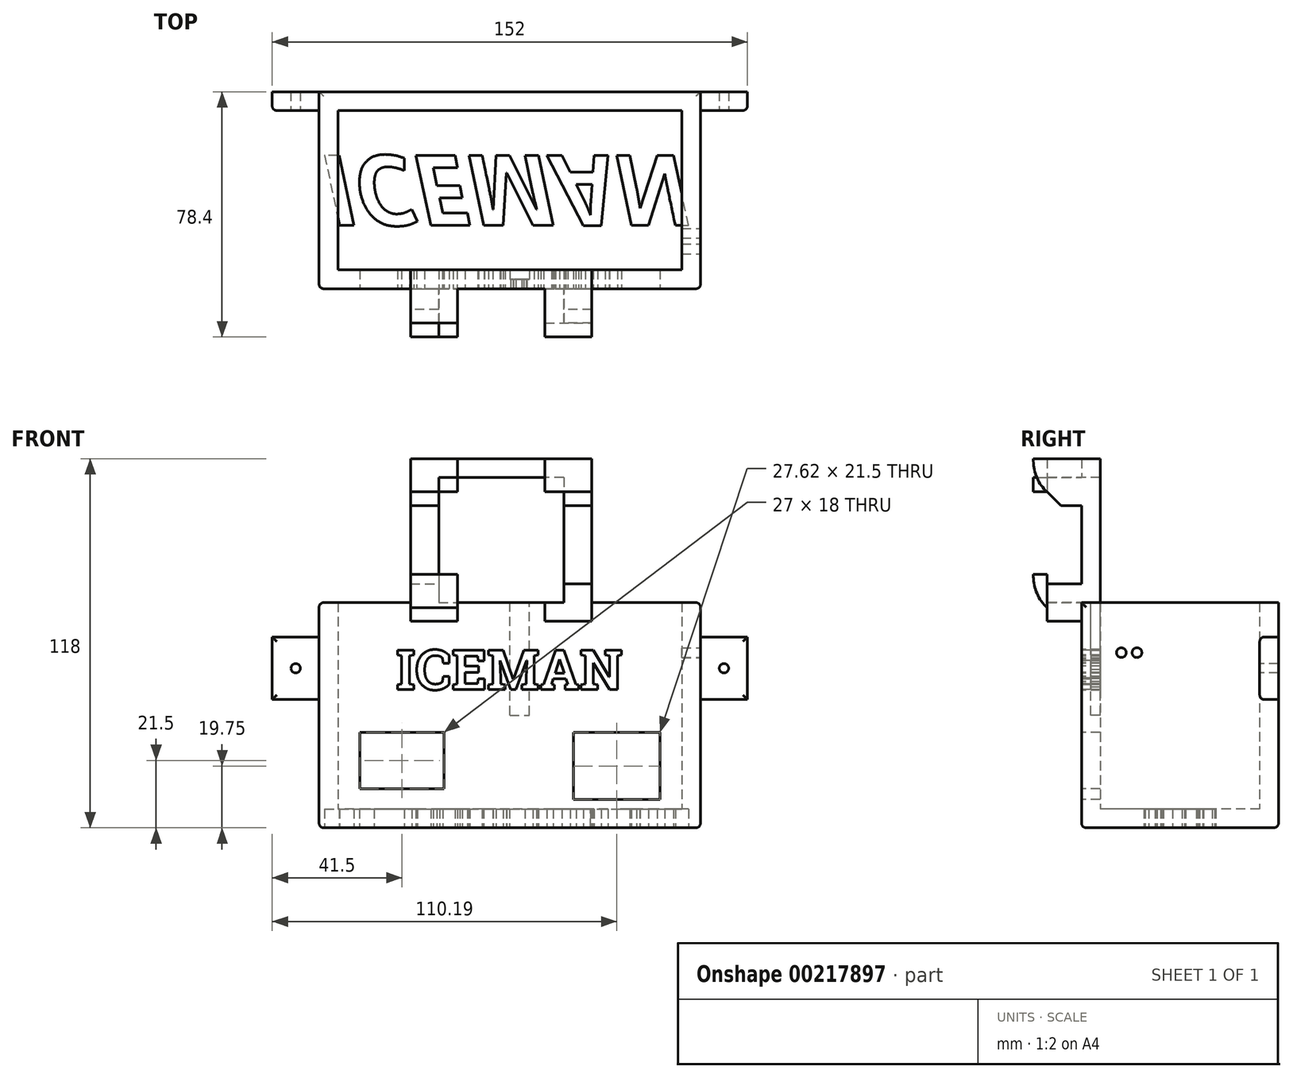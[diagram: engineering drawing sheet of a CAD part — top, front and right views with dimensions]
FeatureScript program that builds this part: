
annotation { "Feature Type Name" : "Feature", "Feature Type Description" : "" }
export const myFeature = defineFeature(function(context is Context, id is Id, definition is map)
    precondition{}
    {
        {
            var Q0;
            Q0=qCreatedBy(makeId("Top.planeOp"),FACE);
            var sketch = newSketch(context, id + "F0", { "sketchPlane" : qUnion([Q0])});
            skLineSegment(sketch, "E0.bottom", {"start": v(-61, 31.5) * mm, "end": v(61, 31.5) * mm});
            skLineSegment(sketch, "E0.top", {"start": v(-61, -31.5) * mm, "end": v(61, -31.5) * mm});
            skLineSegment(sketch, "E0.left", {"start": v(-61, 31.5) * mm, "end": v(-61, -31.5) * mm});
            skLineSegment(sketch, "E0.right", {"start": v(61, 31.5) * mm, "end": v(61, -31.5) * mm});
            skPoint(sketch, "E0.middle", {"position": v(0, 0) * mm});
            skSolve(sketch);
        }
        {
            var Q0;
            Q0 = qSketchRegion(id + "F0", true);
            extrude(context, id + "F1", {"entities" : qUnion([Q0]), "depth" : 6 * mm});
        }
        {
            var Q0;
            Q0=makeQuery(id+"F1.opExtrude","CAP_FACE",FACE,{"disambiguationData":[OSD([sQuery(id+"F0.wireOp",EDGE,"E0.bottom"),sQuery(id+"F0.wireOp",EDGE,"E0.top"),sQuery(id+"F0.wireOp",EDGE,"E0.left"),sQuery(id+"F0.wireOp",EDGE,"E0.right")])],"isStart":false});
            var sketch = newSketch(context, id + "F2", { "sketchPlane" : qUnion([Q0])});
            skLineSegment(sketch, "E1", {"start": v(-55, 25.5) * mm, "end": v(-55, -25.5) * mm});
            skLineSegment(sketch, "E2", {"start": v(-55, -25.5) * mm, "end": v(55, -25.5) * mm});
            skLineSegment(sketch, "E3", {"start": v(55, 25.5) * mm, "end": v(-55, 25.5) * mm});
            skLineSegment(sketch, "E4", {"start": v(55, 25.5) * mm, "end": v(55, -25.5) * mm});
            skPoint(sketch, "E5.orphan", {"position": v(55, -31.5) * mm});
            skLineSegment(sketch, "E6.bottom", {"start": v(-61, 31.5) * mm, "end": v(61, 31.5) * mm});
            skLineSegment(sketch, "E6.top", {"start": v(-61, -31.5) * mm, "end": v(61, -31.5) * mm});
            skLineSegment(sketch, "E6.left", {"start": v(-61, 31.5) * mm, "end": v(-61, -31.5) * mm});
            skLineSegment(sketch, "E6.right", {"start": v(61, 31.5) * mm, "end": v(61, -31.5) * mm});
            skSolve(sketch);
        }
        {
            var Q0;
            Q0 = qSketchRegion(id + "F2", true);
            extrude(context, id + "F3", {"entities" : qUnion([Q0]), "operationType" : NewBodyOperationType.ADD, "depth" : 66 * mm});
        }
        {
            var Q0;
            Q0=makeQuery(id+"F3.boolean.opBoolean","MERGE",FACE,{"derivedFrom":[makeQuery(id+"F1.opExtrude","SWEPT_FACE",FACE,{"disambiguationData":[OSD([sQuery(id+"F0.wireOp",EDGE,"E0.top")])]}),makeQuery(id+"F3.opExtrude","SWEPT_FACE",FACE,{"disambiguationData":[OSD([sQuery(id+"F2.wireOp",EDGE,"E6.top")])]})]});
            var sketch = newSketch(context, id + "F4", { "sketchPlane" : qUnion([Q0])});
            skLineSegment(sketch, "E7.bottom", {"start": v(48, 30.5) * mm, "end": v(20.38, 30.5) * mm});
            skLineSegment(sketch, "E7.top", {"start": v(48, 9) * mm, "end": v(20.38, 9) * mm});
            skLineSegment(sketch, "E7.left", {"start": v(48, 30.5) * mm, "end": v(48, 9) * mm});
            skLineSegment(sketch, "E7.right", {"start": v(20.38, 30.5) * mm, "end": v(20.38, 9) * mm});
            skLineSegment(sketch, "E8.bottom", {"start": v(-48, 30.5) * mm, "end": v(-21, 30.5) * mm});
            skLineSegment(sketch, "E8.top", {"start": v(-48, 12.5) * mm, "end": v(-21, 12.5) * mm});
            skLineSegment(sketch, "E8.left", {"start": v(-48, 30.5) * mm, "end": v(-48, 12.5) * mm});
            skLineSegment(sketch, "E8.right", {"start": v(-21, 30.5) * mm, "end": v(-21, 12.5) * mm});
            skText(sketch, "E9", { "text": "ICEMAN", "fontName": "RobotoSlab-Bold.ttf"});
            const initialGuessF4  = {"E9": [-0.03643, 0.04416, 1, 0, 0.01284]};
            skSetInitialGuess(sketch, initialGuessF4);
            skSolve(sketch);
        }
        {
            var Q0;
            Q0 = qSketchRegion(id + "F4", true);
            extrude(context, id + "F5", {"entities" : qUnion([Q0]), "operationType" : NewBodyOperationType.REMOVE, "oppositeDirection" : true, "depth" : 6 * mm});
        }
        {
            var Q0;
            Q0=makeQuery(id+"F1.opExtrude","CAP_FACE",FACE,{"disambiguationData":[OSD([sQuery(id+"F0.wireOp",EDGE,"E0.bottom"),sQuery(id+"F0.wireOp",EDGE,"E0.top"),sQuery(id+"F0.wireOp",EDGE,"E0.left"),sQuery(id+"F0.wireOp",EDGE,"E0.right")])],"isStart":true});
            var sketch = newSketch(context, id + "F6", { "sketchPlane" : qUnion([Q0])});
            skPoint(sketch, "E10.bottom.start.orphan", {"position": v(42.45, 0) * mm});
            skText(sketch, "E11", { "text": "ICEMAN", "fontName": "OpenSans-BoldItalic.ttf"});
            const initialGuessF6  = {"E11": [-0.06005, -0.01114, 1, 0, 0.02254]};
            skSetInitialGuess(sketch, initialGuessF6);
            skSolve(sketch);
        }
        {
            var Q0;
            Q0 = qSketchRegion(id + "F6", true);
            extrude(context, id + "F7", {"entities" : qUnion([Q0]), "operationType" : NewBodyOperationType.REMOVE, "oppositeDirection" : true, "depth" : 6 * mm});
        }
        {
            var Q0;
            Q0=makeQuery(id+"F3.boolean.opBoolean","MERGE",FACE,{"derivedFrom":[makeQuery(id+"F1.opExtrude","SWEPT_FACE",FACE,{"disambiguationData":[OSD([sQuery(id+"F0.wireOp",EDGE,"E0.right")])]}),makeQuery(id+"F3.opExtrude","SWEPT_FACE",FACE,{"disambiguationData":[OSD([sQuery(id+"F2.wireOp",EDGE,"E6.right")])]})]});
            var sketch = newSketch(context, id + "F8", { "sketchPlane" : qUnion([Q0])});
            skCircle(sketch, "E12", {"center": v(-18.77, 56) * mm, "radius": 1.55 * mm});
            skLineSegment(sketch, "E13", {"start": v(-18.77, 56) * mm, "end": v(33.66, 56) * mm, "construction": true});
            skCircle(sketch, "E14", {"center": v(-13.77, 56) * mm, "radius": 1.55 * mm, "construction": true});
            skCircle(sketch, "E15", {"center": v(-13.77, 56) * mm, "radius": 1.56 * mm});
            skSolve(sketch);
        }
        {
            var Q0;
            Q0 = qSketchRegion(id + "F8", true);
            extrude(context, id + "F9", {"entities" : qUnion([Q0]), "operationType" : NewBodyOperationType.REMOVE, "oppositeDirection" : true, "depth" : 6 * mm});
        }
        {
            var Q0;
            Q0=makeQuery(id+"F3.boolean.opBoolean","MERGE",FACE,{"derivedFrom":[makeQuery(id+"F1.opExtrude","SWEPT_FACE",FACE,{"disambiguationData":[OSD([sQuery(id+"F0.wireOp",EDGE,"E0.right")])]}),makeQuery(id+"F3.opExtrude","SWEPT_FACE",FACE,{"disambiguationData":[OSD([sQuery(id+"F2.wireOp",EDGE,"E6.right")])]})]});
            var sketch = newSketch(context, id + "F10", { "sketchPlane" : qUnion([Q0])});
            skLineSegment(sketch, "E16.bottom", {"start": v(31.5, 61) * mm, "end": v(25.5, 61) * mm});
            skLineSegment(sketch, "E16.top", {"start": v(31.5, 41) * mm, "end": v(25.5, 41) * mm});
            skLineSegment(sketch, "E16.left", {"start": v(31.5, 61) * mm, "end": v(31.5, 41) * mm});
            skLineSegment(sketch, "E16.right", {"start": v(25.5, 61) * mm, "end": v(25.5, 41) * mm});
            skLineSegment(sketch, "E17", {"start": v(31.5, 61) * mm, "end": v(-91.25, 61) * mm, "construction": true});
            skLineSegment(sketch, "E18", {"start": v(-91.25, 61) * mm, "end": v(31.5, 41) * mm, "construction": true});
            skLineSegment(sketch, "E19", {"start": v(31.5, 41) * mm, "end": v(-54.22, 41) * mm, "construction": true});
            skLineSegment(sketch, "E20", {"start": v(-54.22, 41) * mm, "end": v(-136.07, 61) * mm, "construction": true});
            skSolve(sketch);
        }
        {
            var Q0;
            Q0 = qSketchRegion(id + "F10", true);
            extrude(context, id + "F11", {"entities" : qUnion([Q0]), "operationType" : NewBodyOperationType.ADD, "depth" : 15 * mm});
        }
        {
            var Q0;
            Q0=makeQuery(id+"F3.boolean.opBoolean","MERGE",FACE,{"derivedFrom":[makeQuery(id+"F1.opExtrude","SWEPT_FACE",FACE,{"disambiguationData":[OSD([sQuery(id+"F0.wireOp",EDGE,"E0.left")])]}),makeQuery(id+"F3.opExtrude","SWEPT_FACE",FACE,{"disambiguationData":[OSD([sQuery(id+"F2.wireOp",EDGE,"E6.left")])]})]});
            var sketch = newSketch(context, id + "F12", { "sketchPlane" : qUnion([Q0])});
            skLineSegment(sketch, "E21.bottom", {"start": v(-31.5, 61) * mm, "end": v(-25.5, 61) * mm});
            skLineSegment(sketch, "E21.top", {"start": v(-31.5, 41) * mm, "end": v(-25.5, 41) * mm});
            skLineSegment(sketch, "E21.left", {"start": v(-31.5, 61) * mm, "end": v(-31.5, 41) * mm});
            skLineSegment(sketch, "E21.right", {"start": v(-25.5, 61) * mm, "end": v(-25.5, 41) * mm});
            skSolve(sketch);
        }
        {
            var Q0;
            Q0 = qSketchRegion(id + "F12", true);
            extrude(context, id + "F13", {"entities" : qUnion([Q0]), "operationType" : NewBodyOperationType.ADD, "depth" : 15 * mm});
        }
        {
            var Q0;
            Q0=makeQuery(id+"F13.opExtrude","SWEPT_FACE",FACE,{"disambiguationData":[OSD([sQuery(id+"F12.wireOp",EDGE,"E21.right")])]});
            var sketch = newSketch(context, id + "F14", { "sketchPlane" : qUnion([Q0])});
            skCircle(sketch, "E22", {"center": v(-68.5, 51) * mm, "radius": 1.5 * mm});
            skPoint(sketch, "E22.centerSnap0", {"position": v(-68.5, 61) * mm});
            skPoint(sketch, "E22.centerSnap1", {"position": v(-76, 51) * mm});
            skSolve(sketch);
        }
        {
            var Q0;
            Q0 = qSketchRegion(id + "F14", true);
            extrude(context, id + "F15", {"entities" : qUnion([Q0]), "operationType" : NewBodyOperationType.REMOVE, "endBound" : BoundingType.THROUGH_ALL, "oppositeDirection" : true, "depth" : 25 * mm});
        }
        {
            var Q0;
            Q0=makeQuery(id+"F11.opExtrude","SWEPT_FACE",FACE,{"disambiguationData":[OSD([sQuery(id+"F10.wireOp",EDGE,"E16.right")])]});
            var sketch = newSketch(context, id + "F16", { "sketchPlane" : qUnion([Q0])});
            skCircle(sketch, "E23", {"center": v(68.5, 51) * mm, "radius": 1.5 * mm});
            skPoint(sketch, "E23.centerSnap0", {"position": v(68.5, 61) * mm});
            skPoint(sketch, "E23.centerSnap1", {"position": v(76, 51) * mm});
            skSolve(sketch);
        }
        {
            var Q0;
            Q0 = qSketchRegion(id + "F16", true);
            extrude(context, id + "F17", {"entities" : qUnion([Q0]), "operationType" : NewBodyOperationType.ADD, "endBound" : BoundingType.THROUGH_ALL, "depth" : 25 * mm});
        }
        {
            var Q0;
            Q0=makeQuery(id+"F17.opExtrude","CAP_FACE",FACE,{"disambiguationData":[OSD([sQuery(id+"F16.wireOp",EDGE,"E23")])],"isStart":false});
            extrude(context, id + "F18", {"entities" : qUnion([Q0]), "operationType" : NewBodyOperationType.REMOVE, "endBound" : BoundingType.THROUGH_ALL, "oppositeDirection" : true, "depth" : 25 * mm});
        }
        {
            var Q0;
            Q0=makeQuery(id+"F3.opExtrude","CAP_FACE",FACE,{"disambiguationData":[OSD([sQuery(id+"F2.wireOp",EDGE,"E1"),sQuery(id+"F2.wireOp",EDGE,"E2"),sQuery(id+"F2.wireOp",EDGE,"E3"),sQuery(id+"F2.wireOp",EDGE,"E4"),sQuery(id+"F2.wireOp",EDGE,"E6.bottom"),sQuery(id+"F2.wireOp",EDGE,"E6.top"),sQuery(id+"F2.wireOp",EDGE,"E6.left"),sQuery(id+"F2.wireOp",EDGE,"E6.right")])],"isStart":false});
            var sketch = newSketch(context, id + "F19", { "sketchPlane" : qUnion([Q0])});
            skLineSegment(sketch, "E24.bottom", {"start": v(0, -25.5) * mm, "end": v(6.26, -25.5) * mm});
            skLineSegment(sketch, "E24.top", {"start": v(0, -28.5) * mm, "end": v(6.26, -28.5) * mm});
            skLineSegment(sketch, "E24.left", {"start": v(0, -25.5) * mm, "end": v(0, -28.5) * mm});
            skLineSegment(sketch, "E24.right", {"start": v(6.26, -25.5) * mm, "end": v(6.26, -28.5) * mm});
            skSolve(sketch);
        }
        {
            var Q0;
            Q0=makeQuery(id+"F19.imprint","IMPRINT",FACE,{"disambiguationData":[TD([[makeQuery(id+"F19.imprint","IMPRINT",EDGE,{"derivedFrom":sQuery(id+"F19.wireOp",EDGE,"E24.bottom")}),-1.0]])]});
            extrude(context, id + "F20", {"entities" : qUnion([Q0]), "operationType" : NewBodyOperationType.REMOVE, "oppositeDirection" : true, "depth" : 36 * mm});
        }
        {
            var Q0;
            Q0=makeQuery(id+"F3.opExtrude","CAP_FACE",FACE,{"disambiguationData":[OSD([sQuery(id+"F2.wireOp",EDGE,"E1"),sQuery(id+"F2.wireOp",EDGE,"E2"),sQuery(id+"F2.wireOp",EDGE,"E3"),sQuery(id+"F2.wireOp",EDGE,"E4"),sQuery(id+"F2.wireOp",EDGE,"E6.bottom"),sQuery(id+"F2.wireOp",EDGE,"E6.top"),sQuery(id+"F2.wireOp",EDGE,"E6.left"),sQuery(id+"F2.wireOp",EDGE,"E6.right")])],"isStart":false});
            var sketch = newSketch(context, id + "F21", { "sketchPlane" : qUnion([Q0])});
            skLineSegment(sketch, "E25.bottom", {"start": v(17.26, -25.5) * mm, "end": v(26.26, -25.5) * mm});
            skLineSegment(sketch, "E25.top", {"start": v(17.26, -31.5) * mm, "end": v(26.26, -31.5) * mm});
            skLineSegment(sketch, "E25.left", {"start": v(17.26, -25.5) * mm, "end": v(17.26, -31.5) * mm});
            skLineSegment(sketch, "E25.right", {"start": v(26.26, -25.5) * mm, "end": v(26.26, -31.5) * mm});
            skLineSegment(sketch, "E26.bottom", {"start": v(-31.74, -25.5) * mm, "end": v(-22.74, -25.5) * mm});
            skLineSegment(sketch, "E26.top", {"start": v(-31.74, -31.5) * mm, "end": v(-22.74, -31.5) * mm});
            skLineSegment(sketch, "E26.left", {"start": v(-31.74, -25.5) * mm, "end": v(-31.74, -31.5) * mm});
            skLineSegment(sketch, "E26.right", {"start": v(-22.74, -25.5) * mm, "end": v(-22.74, -31.5) * mm});
            skSolve(sketch);
        }
        {
            var Q0;
            Q0 = qSketchRegion(id + "F21", true);
            extrude(context, id + "F22", {"entities" : qUnion([Q0]), "operationType" : NewBodyOperationType.ADD, "depth" : 46 * mm});
        }
        {
            var Q0;
            Q0=makeQuery(id+"F22.opExtrude","SWEPT_FACE",FACE,{"disambiguationData":[OSD([sQuery(id+"F21.wireOp",EDGE,"E26.right")])]});
            var sketch = newSketch(context, id + "F23", { "sketchPlane" : qUnion([Q0])});
            skLineSegment(sketch, "E27.bottom", {"start": v(-25.5, 118) * mm, "end": v(-31.5, 118) * mm});
            skLineSegment(sketch, "E27.top", {"start": v(-25.5, 112) * mm, "end": v(-31.5, 112) * mm});
            skLineSegment(sketch, "E27.left", {"start": v(-25.5, 118) * mm, "end": v(-25.5, 112) * mm});
            skLineSegment(sketch, "E27.right", {"start": v(-31.5, 118) * mm, "end": v(-31.5, 112) * mm});
            skSolve(sketch);
        }
        {
            var Q0;
            Q0 = qSketchRegion(id + "F23", true);
            extrude(context, id + "F24", {"entities" : qUnion([Q0]), "operationType" : NewBodyOperationType.ADD, "depth" : 44 * mm});
        }
        {
            var Q0;
            {var subQ2=sQuery(id+"F0.wireOp",EDGE,"E0.left");var subQ3=sQuery(id+"F0.wireOp",EDGE,"E0.top");var subQ5=sQuery(id+"F2.wireOp",EDGE,"E6.top");Q0=makeQuery(id+"F24.boolean.opBoolean","MERGE",FACE,{"derivedFrom":[makeQuery(id+"F22.boolean.opBoolean","MERGE",FACE,{"derivedFrom":[makeQuery(id+"F5.boolean.opBoolean","SPLIT",FACE,{"disambiguationData":[TD([makeQuery(id+"F1.opExtrude","SWEPT_FACE",FACE,{"disambiguationData":[OSD([subQ2])]})])],"derivedFrom":makeQuery(id+"F3.boolean.opBoolean","MERGE",FACE,{"derivedFrom":[makeQuery(id+"F1.opExtrude","SWEPT_FACE",FACE,{"disambiguationData":[OSD([subQ3])]}),makeQuery(id+"F3.opExtrude","SWEPT_FACE",FACE,{"disambiguationData":[OSD([subQ5])]})]})}),makeQuery(id+"F22.opExtrude","SWEPT_FACE",FACE,{"disambiguationData":[OSD([sQuery(id+"F21.wireOp",EDGE,"E25.top")])]}),makeQuery(id+"F22.opExtrude","SWEPT_FACE",FACE,{"disambiguationData":[OSD([sQuery(id+"F21.wireOp",EDGE,"E26.top")])]})]}),makeQuery(id+"F24.opExtrude","SWEPT_FACE",FACE,{"disambiguationData":[OSD([sQuery(id+"F23.wireOp",EDGE,"E27.right")])]})]});}
            var sketch = newSketch(context, id + "F25", { "sketchPlane" : qUnion([Q0])});
            skLineSegment(sketch, "E28.bottom", {"start": v(-31.74, 118) * mm, "end": v(-22.74, 118) * mm});
            skLineSegment(sketch, "E28.top", {"start": v(-31.74, 103) * mm, "end": v(-22.74, 103) * mm});
            skLineSegment(sketch, "E28.left", {"start": v(-31.74, 118) * mm, "end": v(-31.74, 103) * mm});
            skLineSegment(sketch, "E28.right", {"start": v(-22.74, 118) * mm, "end": v(-22.74, 103) * mm});
            skLineSegment(sketch, "E29", {"start": v(-2.74, 118) * mm, "end": v(-2.74, 63.41) * mm, "construction": true});
            skPoint(sketch, "E29.endSnap0", {"position": v(-2.74, 72) * mm});
            skLineSegment(sketch, "E30.MirrorCS", {"start": v(26.26, 103) * mm, "end": v(17.26, 103) * mm});
            skLineSegment(sketch, "E31.top", {"start": v(-31.74, 78) * mm, "end": v(-22.74, 78) * mm});
            skLineSegment(sketch, "E31.left", {"start": v(-31.74, 72) * mm, "end": v(-31.74, 78) * mm});
            skLineSegment(sketch, "E31.right", {"start": v(-22.74, 72) * mm, "end": v(-22.74, 78) * mm});
            skLineSegment(sketch, "E32.bottom", {"start": v(-22.74, 72) * mm, "end": v(17.26, 72) * mm});
            skLineSegment(sketch, "E32.top", {"start": v(-31.74, 66) * mm, "end": v(26.26, 66) * mm});
            skLineSegment(sketch, "E32.left", {"start": v(-31.74, 72) * mm, "end": v(-31.74, 66) * mm});
            skLineSegment(sketch, "E32.right", {"start": v(26.26, 72) * mm, "end": v(26.26, 66) * mm});
            skLineSegment(sketch, "E33.MirrorCS", {"start": v(26.26, 78) * mm, "end": v(17.26, 78) * mm});
            skLineSegment(sketch, "E34.bottom", {"start": v(-22.74, 72) * mm, "end": v(-16.74, 72) * mm});
            skLineSegment(sketch, "E34.top", {"start": v(-22.74, 66) * mm, "end": v(-16.74, 66) * mm});
            skLineSegment(sketch, "E34.right", {"start": v(-16.74, 72) * mm, "end": v(-16.74, 66) * mm});
            skLineSegment(sketch, "E35.MirrorCS", {"start": v(17.26, 112) * mm, "end": v(17.26, 103) * mm});
            skLineSegment(sketch, "E36.MirrorCS", {"start": v(17.26, 72) * mm, "end": v(17.26, 78) * mm});
            skLineSegment(sketch, "E37.MirrorCS", {"start": v(26.26, 72) * mm, "end": v(26.26, 78) * mm});
            skLineSegment(sketch, "E38.MirrorCS", {"start": v(26.26, 66) * mm, "end": v(11.26, 66) * mm});
            skLineSegment(sketch, "E39.MirrorCS", {"start": v(11.26, 72) * mm, "end": v(11.26, 66) * mm});
            skLineSegment(sketch, "E40.MirrorCS", {"start": v(-16.74, 72) * mm, "end": v(-22.74, 72) * mm});
            skPoint(sketch, "E41.orphan", {"position": v(-31.74, 72) * mm});
            skPoint(sketch, "E42.orphan", {"position": v(26.26, 72) * mm});
            skLineSegment(sketch, "E43.bottom", {"start": v(-22.74, 118) * mm, "end": v(-16.74, 118) * mm});
            skLineSegment(sketch, "E43.top", {"start": v(-22.74, 112) * mm, "end": v(-16.74, 112) * mm});
            skLineSegment(sketch, "E43.right", {"start": v(-16.74, 118) * mm, "end": v(-16.74, 112) * mm});
            skLineSegment(sketch, "E44.bottom", {"start": v(17.26, 118) * mm, "end": v(11.26, 118) * mm});
            skLineSegment(sketch, "E44.top", {"start": v(17.26, 112) * mm, "end": v(11.26, 112) * mm});
            skLineSegment(sketch, "E44.left", {"start": v(17.26, 118) * mm, "end": v(17.26, 112) * mm});
            skLineSegment(sketch, "E44.right", {"start": v(11.26, 118) * mm, "end": v(11.26, 112) * mm});
            skPoint(sketch, "E45.MirrorCS.end.orphan", {"position": v(17.26, 66) * mm});
            skPoint(sketch, "E45.MirrorCS.start.orphan", {"position": v(17.26, 72) * mm});
            skLineSegment(sketch, "E46.trimOffspring", {"start": v(-16.74, 66) * mm, "end": v(-31.74, 66) * mm});
            skSolve(sketch);
        }
        {
            var Q0;
            {var subQ2=sQuery(id+"F25.wireOp",EDGE,"E28.bottom");Q0=makeQuery(id+"F25.imprint","IMPRINT",FACE,{"disambiguationData":[TD([[makeQuery(id+"F25.imprint","IMPRINT",EDGE,{"derivedFrom":subQ2}),-1.0]])]});}
            var Q1;
            {var subQ2=sQuery(id+"F25.wireOp",EDGE,"E43.bottom");Q1=makeQuery(id+"F25.imprint","IMPRINT",FACE,{"disambiguationData":[TD([[makeQuery(id+"F25.imprint","IMPRINT",EDGE,{"derivedFrom":subQ2}),-1.0]])]});}
            var Q2;
            Q2=makeQuery(id+"F25.imprint","IMPRINT",FACE,{"disambiguationData":[TD([[makeQuery(id+"F25.imprint","IMPRINT",EDGE,{"derivedFrom":sQuery(id+"F25.wireOp",EDGE,"E44.bottom")}),-1.0]])]});
            var Q3;
            Q3=makeQuery(id+"F25.imprint","IMPRINT",FACE,{"disambiguationData":[TD([[makeQuery(id+"F25.imprint","IMPRINT",EDGE,{"derivedFrom":sQuery(id+"F25.wireOp",EDGE,"E31.top")}),-1.0]])]});
            var Q4;
            Q4=makeQuery(id+"F25.imprint","IMPRINT",FACE,{"disambiguationData":[TD([[makeQuery(id+"F25.imprint","IMPRINT",EDGE,{"derivedFrom":sQuery(id+"F25.wireOp",EDGE,"E33.MirrorCS")}),1.0]])]});
            var Q5;
            {var subQ4=sQuery(id+"F25.wireOp",EDGE,"E30.MirrorCS");Q5=makeQuery(id+"F25.imprint","IMPRINT",FACE,{"disambiguationData":[TD([[makeQuery(id+"F25.imprint","IMPRINT",EDGE,{"derivedFrom":subQ4}),-1.0]])]});}
            extrude(context, id + "F26", {"entities" : qUnion([Q0, Q1, Q2, Q3, Q4, Q5]), "operationType" : NewBodyOperationType.ADD, "depth" : 11 * mm});
        }
        {
            var Q0;
            Q0=makeQuery(id+"F26.opExtrude","CAP_EDGE",EDGE,{"disambiguationData":[OSD([sQuery(id+"F25.wireOp",EDGE,"E28.top")])],"isStart":false});
            var Q1;
            Q1=makeQuery(id+"F26.opExtrude","CAP_EDGE",EDGE,{"disambiguationData":[OSD([sQuery(id+"F25.wireOp",EDGE,"E30.MirrorCS")])],"isStart":false});
            var Q2;
            Q2=makeQuery(id+"F26.opExtrude","CAP_EDGE",EDGE,{"disambiguationData":[OSD([sQuery(id+"F25.wireOp",EDGE,"E38.MirrorCS")])],"isStart":false});
            var Q3;
            Q3=makeQuery(id+"F26.opExtrude","CAP_EDGE",EDGE,{"disambiguationData":[OSD([sQuery(id+"F25.wireOp",EDGE,"E46.trimOffspring")])],"isStart":false});
            chamfer(context, id + "F27", {"entities" : qUnion([Q0, Q1, Q2, Q3]), "width" : 4.4 * mm, "tangentPropagation" : true});
        }
        {
            var Q0;
            Q0=makeQuery(id+"F26.opExtrude","CAP_FACE",FACE,{"disambiguationData":[OSD([sQuery(id+"F25.wireOp",EDGE,"E28.bottom"),sQuery(id+"F25.wireOp",EDGE,"E28.top"),sQuery(id+"F25.wireOp",EDGE,"E28.left"),sQuery(id+"F25.wireOp",EDGE,"E28.right"),sQuery(id+"F25.wireOp",EDGE,"E43.bottom"),sQuery(id+"F25.wireOp",EDGE,"E43.top"),sQuery(id+"F25.wireOp",EDGE,"E43.right")])],"isStart":false});
            var sketch = newSketch(context, id + "F28", { "sketchPlane" : qUnion([Q0])});
            skLineSegment(sketch, "E47.bottom", {"start": v(-31.74, 118) * mm, "end": v(-16.74, 118) * mm});
            skLineSegment(sketch, "E47.top", {"start": v(-31.74, 107.4) * mm, "end": v(-16.74, 107.4) * mm});
            skLineSegment(sketch, "E47.left", {"start": v(-31.74, 118) * mm, "end": v(-31.74, 107.4) * mm});
            skLineSegment(sketch, "E47.right", {"start": v(-16.74, 118) * mm, "end": v(-16.74, 107.4) * mm});
            skLineSegment(sketch, "E48.bottom", {"start": v(-31.74, 118) * mm, "end": v(26.26, 118) * mm, "construction": true});
            skLineSegment(sketch, "E48.top", {"start": v(-31.74, 70.4) * mm, "end": v(26.26, 70.4) * mm, "construction": true});
            skLineSegment(sketch, "E48.left", {"start": v(-31.74, 118) * mm, "end": v(-31.74, 70.4) * mm, "construction": true});
            skLineSegment(sketch, "E48.right", {"start": v(26.26, 118) * mm, "end": v(26.26, 70.4) * mm, "construction": true});
            skLineSegment(sketch, "E49", {"start": v(-2.74, 118) * mm, "end": v(-2.74, 69.66) * mm, "construction": true});
            skLineSegment(sketch, "E50", {"start": v(-2.74, 69.66) * mm, "end": v(-3.62, 70.4) * mm, "construction": true});
            skLineSegment(sketch, "E51", {"start": v(-31.74, 94.2) * mm, "end": v(35.92, 94.2) * mm, "construction": true});
            skPoint(sketch, "E51.endSnap0", {"position": v(26.26, 94.2) * mm});
            skLineSegment(sketch, "E52.MirrorCS", {"start": v(11.26, 118) * mm, "end": v(11.26, 107.4) * mm});
            skLineSegment(sketch, "E53.MirrorCS", {"start": v(26.26, 107.4) * mm, "end": v(11.26, 107.4) * mm});
            skLineSegment(sketch, "E54.MirrorCS", {"start": v(26.26, 118) * mm, "end": v(-31.74, 118) * mm, "construction": true});
            skLineSegment(sketch, "E55.MirrorCS", {"start": v(-31.74, 81) * mm, "end": v(-16.74, 81) * mm});
            skLineSegment(sketch, "E56.MirrorCS", {"start": v(-16.74, 70.4) * mm, "end": v(-16.74, 81) * mm});
            skLineSegment(sketch, "E57.MirrorCS", {"start": v(11.26, 70.4) * mm, "end": v(11.26, 81) * mm});
            skLineSegment(sketch, "E58.MirrorCS", {"start": v(26.26, 81) * mm, "end": v(11.26, 81) * mm});
            skLineSegment(sketch, "E59.MirrorCS", {"start": v(26.26, 70.4) * mm, "end": v(-31.74, 70.4) * mm, "construction": true});
            skLineSegment(sketch, "E60.top", {"start": v(-31.74, 70.4) * mm, "end": v(-16.74, 70.4) * mm});
            skLineSegment(sketch, "E60.left", {"start": v(-31.74, 81) * mm, "end": v(-31.74, 70.4) * mm});
            skLineSegment(sketch, "E60.right", {"start": v(-16.74, 81) * mm, "end": v(-16.74, 70.4) * mm});
            skLineSegment(sketch, "E61.bottom", {"start": v(11.26, 81) * mm, "end": v(26.26, 81) * mm});
            skLineSegment(sketch, "E61.top", {"start": v(11.26, 70.4) * mm, "end": v(26.26, 70.4) * mm});
            skLineSegment(sketch, "E61.left", {"start": v(11.26, 81) * mm, "end": v(11.26, 70.4) * mm});
            skLineSegment(sketch, "E61.right", {"start": v(26.26, 81) * mm, "end": v(26.26, 70.4) * mm});
            skLineSegment(sketch, "E62.bottom", {"start": v(26.26, 118) * mm, "end": v(11.26, 118) * mm});
            skLineSegment(sketch, "E62.left", {"start": v(26.26, 118) * mm, "end": v(26.26, 107.4) * mm});
            skLineSegment(sketch, "E63.bottom", {"start": v(-16.74, 118) * mm, "end": v(-31.74, 118) * mm});
            skLineSegment(sketch, "E63.top", {"start": v(-16.74, 107.4) * mm, "end": v(-31.74, 107.4) * mm});
            skSolve(sketch);
        }
        {
            var Q0;
            {var subQ4=makeQuery(id+"F26.opExtrude","CAP_EDGE",EDGE,{"disambiguationData":[OSD([sQuery(id+"F25.wireOp",EDGE,"E43.top")])],"isStart":false});Q0=makeQuery(id+"F28.imprint","IMPRINT",FACE,{"disambiguationData":[TD([[makeQuery(id+"F28.imprint","IMPRINT",EDGE,{"derivedFrom":subQ4}),1.0]])]});}
            var Q1;
            Q1=makeQuery(id+"F28.imprint","IMPRINT",FACE,{"disambiguationData":[TD([[makeQuery(id+"F28.imprint","IMPRINT",EDGE,{"derivedFrom":sQuery(id+"F28.wireOp",EDGE,"E62.bottom")}),1.0]])]});
            var Q2;
            {var subQ4=sQuery(id+"F28.wireOp",EDGE,"E63.bottom");Q2=makeQuery(id+"F28.imprint","IMPRINT",FACE,{"disambiguationData":[TD([[makeQuery(id+"F28.imprint","IMPRINT",EDGE,{"derivedFrom":subQ4}),-1.0]])]});}
            var Q3;
            Q3=makeQuery(id+"F28.imprint","IMPRINT",FACE,{"disambiguationData":[TD([[makeQuery(id+"F28.imprint","IMPRINT",EDGE,{"derivedFrom":sQuery(id+"F28.wireOp",EDGE,"E55.MirrorCS")}),-1.0]])]});
            var Q4;
            Q4=makeQuery(id+"F28.imprint","IMPRINT",FACE,{"disambiguationData":[TD([[makeQuery(id+"F28.imprint","IMPRINT",EDGE,{"derivedFrom":sQuery(id+"F28.wireOp",EDGE,"E61.bottom")}),-1.0]])]});
            extrude(context, id + "F29", {"entities" : qUnion([Q0, Q1, Q2, Q3, Q4]), "operationType" : NewBodyOperationType.ADD, "depth" : 4.4 * mm});
        }
        {
            var Q0;
            Q0=makeQuery(id+"F29.opExtrude","CAP_EDGE",EDGE,{"disambiguationData":[OSD([sQuery(id+"F28.wireOp",EDGE,"E60.top")])],"isStart":false});
            var Q1;
            Q1=makeQuery(id+"F29.opExtrude","CAP_EDGE",EDGE,{"disambiguationData":[OSD([sQuery(id+"F28.wireOp",EDGE,"E61.top")])],"isStart":false});
            var Q2;
            Q2=makeQuery(id+"F29.opExtrude","CAP_EDGE",EDGE,{"disambiguationData":[OSD([sQuery(id+"F28.wireOp",EDGE,"E63.top")])],"isStart":false});
            var Q3;
            Q3=makeQuery(id+"F29.opExtrude","CAP_EDGE",EDGE,{"disambiguationData":[OSD([sQuery(id+"F28.wireOp",EDGE,"E53.MirrorCS")])],"isStart":false});
            var Q4;
            {var subQ0=sQuery(id+"F25.wireOp",EDGE,"E46.trimOffspring");Q4=makeQuery(id+"F27.opChamfer","BLEND_EDGE",EDGE,{"blendedFrom":[makeQuery(id+"F26.opExtrude","CAP_EDGE",EDGE,{"disambiguationData":[OSD([subQ0])],"isStart":false}),makeQuery(id+"F26.opExtrude","SWEPT_FACE",FACE,{"disambiguationData":[OSD([subQ0])]})],"blendedInto":[makeQuery(id+"F26.opExtrude","SWEPT_FACE",FACE,{"disambiguationData":[OSD([subQ0])]})]});}
            var Q5;
            {var subQ0=sQuery(id+"F25.wireOp",EDGE,"E38.MirrorCS");Q5=makeQuery(id+"F27.opChamfer","BLEND_EDGE",EDGE,{"blendedFrom":[makeQuery(id+"F26.opExtrude","CAP_EDGE",EDGE,{"disambiguationData":[OSD([subQ0])],"isStart":false}),makeQuery(id+"F26.opExtrude","SWEPT_FACE",FACE,{"disambiguationData":[OSD([subQ0])]})],"blendedInto":[makeQuery(id+"F26.opExtrude","SWEPT_FACE",FACE,{"disambiguationData":[OSD([subQ0])]})]});}
            fillet(context, id + "F30", {"entities" : qUnion([Q0, Q1, Q2, Q3, Q4, Q5]), "radius" : 13.35 * mm, "tangentPropagation" : true, "allowEdgeOverflow" : false});
        }
        {
            var Q0;
            Q0=makeQuery(id+"F1.opExtrude","CAP_EDGE",EDGE,{"disambiguationData":[OSD([sQuery(id+"F0.wireOp",EDGE,"E0.bottom")])],"isStart":true});
            var Q1;
            Q1=makeQuery(id+"F1.opExtrude","CAP_EDGE",EDGE,{"disambiguationData":[OSD([sQuery(id+"F0.wireOp",EDGE,"E0.right")])],"isStart":true});
            var Q2;
            Q2=makeQuery(id+"F1.opExtrude","CAP_EDGE",EDGE,{"disambiguationData":[OSD([sQuery(id+"F0.wireOp",EDGE,"E0.top")])],"isStart":true});
            var Q3;
            Q3=makeQuery(id+"F1.opExtrude","CAP_EDGE",EDGE,{"disambiguationData":[OSD([sQuery(id+"F0.wireOp",EDGE,"E0.left")])],"isStart":true});
            var Q4;
            Q4=makeQuery(id+"F13.opExtrude","SWEPT_EDGE",EDGE,{"disambiguationData":[OSD([sQuery(id+"F12.wireOp",EDGE,"E21.top"),sQuery(id+"F12.wireOp",EDGE,"E21.right")])]});
            var Q5;
            Q5=makeQuery(id+"F13.opExtrude","CAP_EDGE",EDGE,{"disambiguationData":[OSD([sQuery(id+"F12.wireOp",EDGE,"E21.right")])],"isStart":false});
            var Q6;
            Q6=makeQuery(id+"F13.opExtrude","SWEPT_EDGE",EDGE,{"disambiguationData":[OSD([sQuery(id+"F12.wireOp",EDGE,"E21.bottom"),sQuery(id+"F12.wireOp",EDGE,"E21.right")])]});
            var Q7;
            Q7=makeQuery(id+"F11.opExtrude","CAP_EDGE",EDGE,{"disambiguationData":[OSD([sQuery(id+"F10.wireOp",EDGE,"E16.right")])],"isStart":false});
            var Q8;
            Q8=makeQuery(id+"F11.opExtrude","SWEPT_EDGE",EDGE,{"disambiguationData":[OSD([sQuery(id+"F10.wireOp",EDGE,"E16.bottom"),sQuery(id+"F10.wireOp",EDGE,"E16.right")])]});
            var Q9;
            Q9=makeQuery(id+"F11.opExtrude","SWEPT_EDGE",EDGE,{"disambiguationData":[OSD([sQuery(id+"F10.wireOp",EDGE,"E16.top"),sQuery(id+"F10.wireOp",EDGE,"E16.right")])]});
            var Q10;
            Q10=makeQuery(id+"F3.boolean.opBoolean","MERGE",EDGE,{"derivedFrom":[makeQuery(id+"F1.opExtrude","SWEPT_EDGE",EDGE,{"disambiguationData":[OSD([sQuery(id+"F0.wireOp",EDGE,"E0.top"),sQuery(id+"F0.wireOp",EDGE,"E0.right")])]}),makeQuery(id+"F3.opExtrude","SWEPT_EDGE",EDGE,{"disambiguationData":[OSD([sQuery(id+"F2.wireOp",EDGE,"E6.top"),sQuery(id+"F2.wireOp",EDGE,"E6.right")])]})]});
            var Q11;
            Q11=makeQuery(id+"F3.opExtrude","CAP_EDGE",EDGE,{"disambiguationData":[OSD([sQuery(id+"F2.wireOp",EDGE,"E6.right")])],"isStart":false});
            var Q12;
            Q12=makeQuery(id+"F3.boolean.opBoolean","MERGE",EDGE,{"derivedFrom":[makeQuery(id+"F1.opExtrude","SWEPT_EDGE",EDGE,{"disambiguationData":[OSD([sQuery(id+"F0.wireOp",EDGE,"E0.top"),sQuery(id+"F0.wireOp",EDGE,"E0.left")])]}),makeQuery(id+"F3.opExtrude","SWEPT_EDGE",EDGE,{"disambiguationData":[OSD([sQuery(id+"F2.wireOp",EDGE,"E6.top"),sQuery(id+"F2.wireOp",EDGE,"E6.left")])]})]});
            var Q13;
            {var subQ1=sQuery(id+"F2.wireOp",EDGE,"E6.top");Q13=makeQuery(id+"F22.boolean.opBoolean","SPLIT",EDGE,{"disambiguationData":[TD([makeQuery(id+"F1.opExtrude","SWEPT_FACE",FACE,{"disambiguationData":[OSD([sQuery(id+"F0.wireOp",EDGE,"E0.left")])]})])],"derivedFrom":makeQuery(id+"F3.opExtrude","CAP_EDGE",EDGE,{"disambiguationData":[OSD([subQ1])],"isStart":false})});}
            var Q14;
            Q14=makeQuery(id+"F3.opExtrude","CAP_EDGE",EDGE,{"disambiguationData":[OSD([sQuery(id+"F2.wireOp",EDGE,"E6.left")])],"isStart":false});
            fillet(context, id + "F31", {"entities" : qUnion([Q0, Q1, Q2, Q3, Q4, Q5, Q6, Q7, Q8, Q9, Q10, Q11, Q12, Q13, Q14]), "radius" : 1.45 * mm, "tangentPropagation" : true, "allowEdgeOverflow" : false});
        }
    });
